# Revit family: Haworth_Janus_Quinta_Table_Dining
name_source: partatom
category: Furniture
revit_build: Autodesk Revit 2018 (Build: 20170223_1515(x64)
units: mm (PartAtom-declared; Revit-internal decimal feet)

## family parameters
Always vertical = Yes
Cut with Voids When Loaded = No
OmniClass Number = 23.40.70.14.64.21
OmniClass Title = Systems Furniture
Room Calculation Point = No
Shared = No
Work Plane-Based = No

## types (2) — shared parameters
Actual Depth = 39 1/4"
Actual Height = 29 1/2"
Assembly Code = E2020200
Glide Finish = Haworth _ Polymer _ Black
Leg Height = 29 1/2"
Manufacturer = Haworth
Revision Number = 2
Size = Verify Final Dim. w/ Haworth
Top Finish = Haworth _ Glass _ Sanded
URL = http://www.haworth.com
URL - Product = https://www.haworth.com
Warranty = https://www.haworth.com

## per-type parameters (varying)
| type | Actual Width | Description | Model | Rectangle | Square | Top Thickness |
| HCJC-QN-TDQ39-WG - Square | 39 1/4" | Haworth Janus Quinta - Square Dining Table | HCJC-QN-TDQ39-WG | No | Yes | 1 187/256" |
| HCJC-QN-TDR79-WG - Rectangle | 78 3/4" | Haworth Janus Quinta - Rectangle Dining Table | HCJC-QN-TDR79-WG | Yes | No | 1 221/256" |

## geometry (parser evidence)
native form markers: Sweep x2
no freeform markers — native parametric forms only
